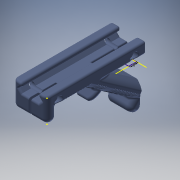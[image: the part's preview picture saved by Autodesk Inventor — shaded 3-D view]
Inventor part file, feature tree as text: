
AUTODESK INVENTOR PART (.ipt)
format: ipt  version: 2016 (Build 200138000, 138)  size: 5,549,056 bytes
history: native  units: mm
features: sketch x24, projected_geometry x24, extrude x23, fillet x21, plane x8, other x2, chamfer x2, revolve x1
ambient origin geometry x8: Origin, YZ Plane, XZ Plane, XY Plane, X Axis, Y Axis, Z Axis, Center Point
bodies: Solid1 (feature_tree)
feature tree (105):
  extrude  "Extrusion1"  Depth=35.0mm
  extrude  "Extrusion2"  Depth=10.0mm
  extrude  "Extrusion3"  Depth=12.0mm
  other  "Work Axis2"
  other  "Work Point2"
  plane  "Work Plane2"
  extrude  "Extrusion5"  Depth=12.0mm
  sketch  "Sketch9"  dims[d14=15.0mm d15=10.0mm d16=15.0mm d17=0.0mm]
  extrude  "Extrusion4"  TaperAngle=90.0deg  [1 undecoded]
  plane  "Work Plane3"
  plane  "Work Plane5"
  extrude  "Extrusion8"  Depth=10.0mm
  fillet  "Fillet3"  Radius=15.0mm
  extrude  "Extrusion9"  Depth=10.0mm
  fillet  "Fillet5"  Radius=130.0mm
  fillet  "Fillet6"  Radius=35.531179mm
  fillet  "Fillet7"  Radius=18.5mm
  fillet  "Fillet8"  Radius=18.5mm
  fillet  "Fillet9"  Radius=7.5mm
  extrude  "Extrusion10"  Depth=36.0mm TaperAngle=0.0deg
  fillet  "Fillet10"  Radius=35.75mm
  fillet  "Fillet11"  [1 undecoded]
  fillet  "Fillet12"  Radius=34.0mm
  plane  "Work Plane4"
  extrude  "Extrusion11"  Depth=5.0mm
  extrude  "Extrusion12"  Depth=13.5mm TaperAngle=0.0deg
  extrude  "Extrusion13"  Depth=5.0mm
  fillet  "Fillet13"  Radius=2.0mm
  fillet  "Fillet14"  Radius=2.0mm
  fillet  "Fillet15"  Radius=2.0mm
  sketch  "Sketch22"  dims[d113=8.5mm d114=8.5mm]
  extrude  "Extrusion14"  Depth=9.0mm
  extrude  "Extrusion15"  Depth=8.5mm
  extrude  "Extrusion16"  Depth=3.0mm
  fillet  "Fillet16"  [1 undecoded]
  extrude  "Extrusion17"  Depth=2.0mm
  extrude  "Extrusion18"  Depth=1.0mm
  plane  "Work Plane6"
  extrude  "Extrusion19"  Depth=2.0mm
  sketch  "Sketch27"  dims[d128=13.5mm d129=0.0mm d131=5.0mm]
  extrude  "Extrusion21"  Depth=5.0mm
  extrude  "Extrusion22"  Depth=2.0mm
  fillet  "Fillet17"  Radius=8.0mm
  fillet  "Fillet18"  Radius=8.0mm
  fillet  "Fillet19"  Radius=5.0mm
  extrude  "Extrusion23"  Depth=5.0mm TaperAngle=0.0deg
  extrude  "Extrusion24"  Depth=0.5mm
  fillet  "Fillet20"  Radius=0.5mm
  chamfer  "Chamfer3"  Distance=55.0mm
  chamfer  "Chamfer4"  Distance=4.0mm
  fillet  "Fillet22"  Radius=4.0mm
  extrude  "Extrusion25"  Depth=1.0mm TaperAngle=0.0deg
  plane  "Work Plane7"
  sketch  "Sketch33"  dims[d145=1.0mm]
  plane  "Work Plane8"
  plane  "Work Plane9"
  extrude  "Extrusion27"  Depth=1.0mm
  revolve  "Revolution1"  [1 undecoded]
  fillet  "Fillet30"  Radius=5.0mm
  fillet  "Fillet31"  Radius=5.0mm
  fillet  "Fillet32"  Radius=2.5mm
  sketch  "Sketch1"  dims[d0=135.0mm d1=35.0mm]
  sketch  "Sketch2"  dims[d2=10.0mm d3=0.0mm d4=10.0mm]
  projected_geometry  "Projected Loop1"
  sketch  "Sketch3"  dims[d5=15.0mm d6=0.0mm d7=12.0mm]
  projected_geometry  "Projected Loop2"
  sketch  "Sketch4"  dims[d10=9.599311mm d11=12.0mm]
  projected_geometry  "Projected Loop3"
  sketch  "Sketch5"  dims[d12=35.0mm d13=90.0deg]
  sketch  "Sketch12"  dims[d18=17.0mm d19=10.0mm d20=130.0mm d21=0.0mm d23=35.531179mm d24=18.5mm d25=18.5mm d26=7.5mm]
  projected_geometry  "Projected Loop11"
  sketch  "Sketch14"  dims[d27=7.5mm d28=36.0mm d29=0.0mm d30=35.75mm d31=0.0mm d32=-5.0mm d44=34.0mm d45=0.0mm]
  sketch  "Sketch18"  dims[d46=5.0mm d48=5.0mm]
  projected_geometry  "Projected Loop26"
  sketch  "Sketch19"  dims[d49=5.0mm d50=13.5mm d51=0.0mm]
  sketch  "Sketch20"  dims[d60=5.0mm d61=5.0mm d62=2.0mm d63=2.0mm d64=2.0mm]
  sketch  "Sketch21"  dims[d67=2.0mm d112=9.0mm]
  sketch  "Sketch23"  dims[d115=3.0mm d116=3.0mm d117=45.0deg]
  projected_geometry  "Projected Loop28"
  sketch  "Sketch24"  dims[d118=13.5mm d119=0.0mm d120=2.0mm]
  projected_geometry  "Projected Loop29"
  projected_geometry  "Projected Loop30"
  projected_geometry  "Projected Loop31"
  sketch  "Sketch25"  dims[d121=2.0mm d122=1.0mm]
  sketch  "Sketch26"  dims[d123=-17.5mm d125=2.0mm]
  projected_geometry  "Projected Loop32"
  projected_geometry  "Projected Loop33"
  projected_geometry  "Projected Loop34"
  projected_geometry  "Projected Loop35"
  sketch  "Sketch28"  dims[d132=5.0mm d133=2.0mm d134=8.0mm d135=8.0mm d136=5.0mm d137=0.0mm]
  projected_geometry  "Projected Loop36"
  sketch  "Sketch29"  dims[d138=4.25mm d139=5.0mm d140=0.0mm]
  sketch  "Sketch30"  dims[d141=0.5mm d142=0.5mm d143=0.5mm]
  sketch  "Sketch32"  dims[d144=25.0mm]
  projected_geometry  "Projected Loop37"
  projected_geometry  "Projected Loop38"
  projected_geometry  "Projected Loop39"
  sketch  "Sketch35"  dims[d146=1.0mm d147=55.0mm d148=0.0mm d149=4.0mm d150=4.0mm d151=15.0mm d152=0.0mm d153=1.0mm d154=5.0mm d155=5.0mm d156=5.0mm d157=0.0mm d158=2.5mm d160=1.0mm d161=1.5mm d163=1.0mm d164=1.0mm d165=1.5mm d166=1.0mm d167=1.0mm d168=1.5mm d169=1.0mm d170=1.0mm d171=1.5mm d172=1.0mm d173=1.0mm d174=1.5mm d175=1.0mm d176=1.0mm d177=1.5mm d178=1.0mm d179=1.0mm d180=1.5mm d181=1.0mm d182=1.0mm d183=1.5mm d184=1.0mm d185=1.0mm d186=1.5mm d187=1.0mm d188=1.0mm d189=1.5mm d190=1.0mm d191=1.0mm d192=1.5mm d193=1.0mm d194=1.0mm d195=1.5mm d196=1.0mm d197=1.0mm d198=1.5mm d199=1.0mm d200=1.0mm d201=1.5mm d202=1.0mm d203=1.0mm d204=1.5mm d205=1.0mm d206=1.0mm d207=1.5mm d208=1.0mm d209=1.0mm d210=1.5mm d211=1.0mm d212=6.5mm d213=0.0mm d214=1.5mm d215=50.75mm d216=0.0mm d217=1.0mm d218=1.5mm d219=1.0mm d220=90.0deg d221=1.5mm d222=1.0mm d223=1.5mm d224=1.0mm d225=1.0mm d226=1.0mm d227=1.5mm d228=1.0mm d229=1.5mm d230=1.0mm d231=1.0mm d232=1.0mm d233=1.5mm d234=1.0mm d235=1.5mm d236=1.0mm d237=1.0mm d238=1.0mm d239=1.5mm d240=1.0mm d241=1.5mm d242=1.0mm d243=1.0mm d244=1.0mm d245=1.5mm d246=1.0mm d247=1.5mm d248=1.0mm d249=1.0mm d250=1.0mm d251=1.5mm d252=1.0mm d253=1.5mm d254=1.0mm d255=1.0mm d256=1.0mm d257=1.5mm d258=1.0mm d259=1.5mm d260=1.0mm d261=1.0mm d262=1.0mm d263=1.5mm d264=1.0mm d265=1.5mm d266=1.0mm d267=1.0mm d268=1.0mm d269=1.5mm d270=1.0mm d271=1.5mm d272=1.0mm d273=1.0mm d274=1.0mm d275=1.5mm d276=1.0mm d277=1.5mm d278=1.0mm d279=1.0mm d280=1.0mm d281=1.5mm d282=1.0mm d283=1.5mm d284=1.0mm d285=7.5mm d286=0.0mm d287=1.5mm d290=3.75mm d291=0.0mm d292=25.5mm d293=0.0mm d294=25.5mm d295=0.0mm d296=4.25mm d297=0.5mm d298=2.25mm d299=0.0mm d300=0.5mm d301=0.5mm d302=4.25mm d303=0.0mm d304=5.0mm d305=0.0mm d306=0.5mm d307=0.0mm d308=0.2mm d309=2.0mm d310=45.0deg d311=0.2mm d312=2.0mm d313=45.0deg d315=1.5mm d316=1.5mm d317=1.5mm d321=49.0mm d322=0.0mm d323=12.0mm d324=76.68602mm d325=-14.0mm d326=8.0mm d333=-55.0mm d334=-42.0mm d335=38.5mm d336=0.0mm d339=6.108652mm d343=2.0mm d344=1.0mm d345=1.0mm]
  projected_geometry  "Project Cut Edges1"
  projected_geometry  "Project Cut Edges2"
  projected_geometry  "Project Cut Edges3"
  projected_geometry  "Project Cut Edges4"
  projected_geometry  "Project Cut Edges5"
  projected_geometry  "Project Cut Edges6"
  projected_geometry  "Project Cut Edges8"
note: 4 required parameter values undecoded (feature->parameter linkage not recoverable at this tier; creation-order binding heuristic only, values carry confidence <= 0.55)